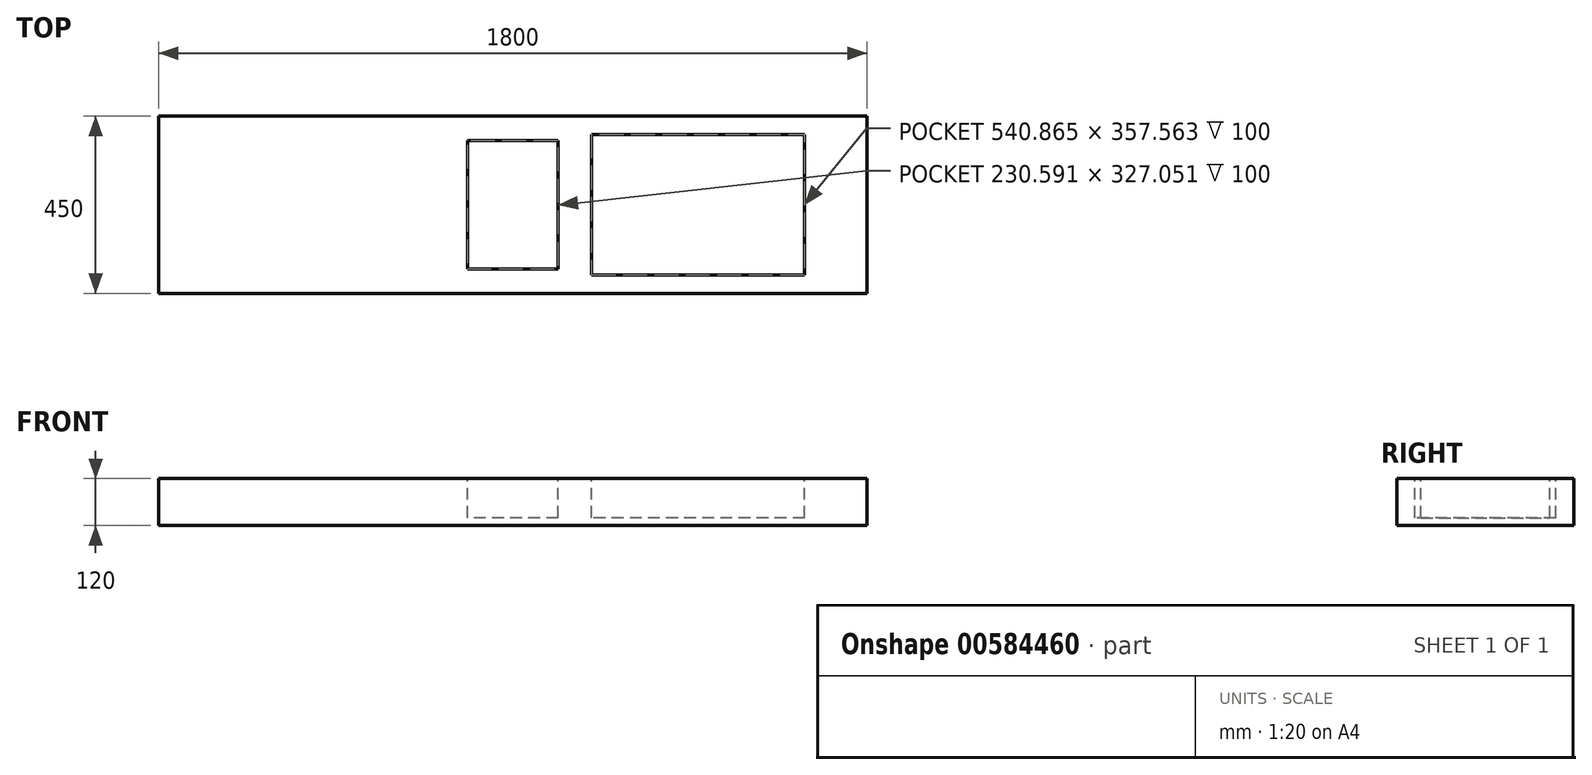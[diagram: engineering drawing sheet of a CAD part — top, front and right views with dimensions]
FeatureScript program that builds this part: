
annotation { "Feature Type Name" : "Feature", "Feature Type Description" : "" }
export const myFeature = defineFeature(function(context is Context, id is Id, definition is map)
    precondition{}
    {
        {
            var Q0;
            Q0=qCreatedBy(makeId("Top.planeOp"),FACE);
            var sketch = newSketch(context, id + "F0", { "sketchPlane" : qUnion([Q0])});
            skLineSegment(sketch, "E0.bottom", {"start": v(900, 225) * mm, "end": v(-900, 225) * mm});
            skLineSegment(sketch, "E0.top", {"start": v(900, -225) * mm, "end": v(-900, -225) * mm});
            skLineSegment(sketch, "E0.left", {"start": v(900, 225) * mm, "end": v(900, -225) * mm});
            skLineSegment(sketch, "E0.right", {"start": v(-900, 225) * mm, "end": v(-900, -225) * mm});
            skPoint(sketch, "E0.middle", {"position": v(0, 0) * mm});
            skSolve(sketch);
        }
        {
            var Q0;
            Q0=makeQuery(id+"F0.imprint","IMPRINT",FACE,{"disambiguationData":[TD([[makeQuery(id+"F0.imprint","IMPRINT",EDGE,{"derivedFrom":sQuery(id+"F0.wireOp",EDGE,"E0.bottom")}),1.0]])]});
            extrude(context, id + "F1", {"entities" : qUnion([Q0]), "endBound" : BoundingType.SYMMETRIC, "depth" : 120 * mm, "offsetDistance" : 25.4 * mm});
        }
        {
            var Q0;
            Q0=makeQuery(id+"F1.opExtrude","CAP_FACE",FACE,{"disambiguationData":[OSD([sQuery(id+"F0.wireOp",EDGE,"E0.bottom"),sQuery(id+"F0.wireOp",EDGE,"E0.top"),sQuery(id+"F0.wireOp",EDGE,"E0.left"),sQuery(id+"F0.wireOp",EDGE,"E0.right")])],"isStart":false});
            var sketch = newSketch(context, id + "F2", { "sketchPlane" : qUnion([Q0])});
            skLineSegment(sketch, "E1.bottom", {"start": v(115.3, -163.53) * mm, "end": v(-115.3, -163.53) * mm});
            skLineSegment(sketch, "E1.top", {"start": v(115.3, 163.53) * mm, "end": v(-115.3, 163.53) * mm});
            skLineSegment(sketch, "E1.left", {"start": v(115.3, -163.53) * mm, "end": v(115.3, 163.53) * mm});
            skLineSegment(sketch, "E1.right", {"start": v(-115.3, -163.53) * mm, "end": v(-115.3, 163.53) * mm});
            skPoint(sketch, "E1.middle", {"position": v(0, 0) * mm});
            skLineSegment(sketch, "E2.bottom", {"start": v(741.43, 178.78) * mm, "end": v(200.57, 178.78) * mm});
            skLineSegment(sketch, "E2.top", {"start": v(741.43, -178.78) * mm, "end": v(200.57, -178.78) * mm});
            skLineSegment(sketch, "E2.left", {"start": v(741.43, 178.78) * mm, "end": v(741.43, -178.78) * mm});
            skLineSegment(sketch, "E2.right", {"start": v(200.57, 178.78) * mm, "end": v(200.57, -178.78) * mm});
            skPoint(sketch, "E2.middle", {"position": v(471, 0) * mm});
            skPoint(sketch, "E2.middle.positionSnap0", {"position": v(115.3, 0) * mm});
            skPoint(sketch, "E2.centerSnap0", {"position": v(115.3, 0) * mm});
            skSolve(sketch);
        }
        {
            var Q0;
            Q0=makeQuery(id+"F2.imprint","IMPRINT",FACE,{"disambiguationData":[TD([[makeQuery(id+"F2.imprint","IMPRINT",EDGE,{"derivedFrom":sQuery(id+"F2.wireOp",EDGE,"E1.bottom")}),-1.0]])]});
            var Q1;
            Q1=makeQuery(id+"F2.imprint","IMPRINT",FACE,{"disambiguationData":[TD([[makeQuery(id+"F2.imprint","IMPRINT",EDGE,{"derivedFrom":sQuery(id+"F2.wireOp",EDGE,"E2.bottom")}),1.0]])]});
            extrude(context, id + "F3", {"entities" : qUnion([Q0, Q1]), "operationType" : NewBodyOperationType.REMOVE, "oppositeDirection" : true, "depth" : 100 * mm, "offsetDistance" : 25.4 * mm});
        }
    });
